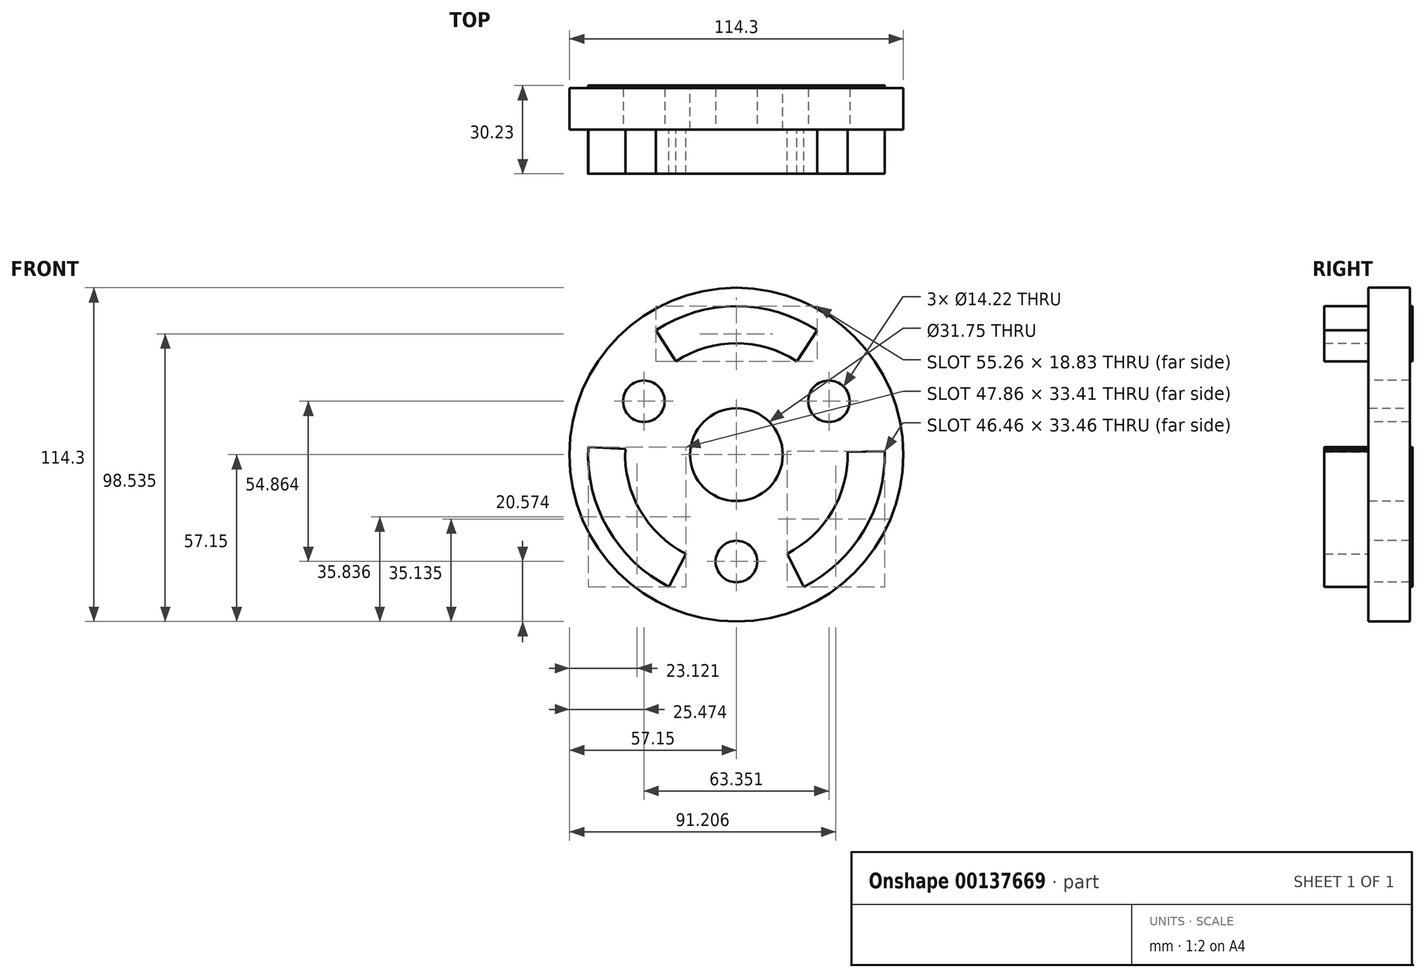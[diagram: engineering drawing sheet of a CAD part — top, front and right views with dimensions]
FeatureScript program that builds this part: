
annotation { "Feature Type Name" : "Feature", "Feature Type Description" : "" }
export const myFeature = defineFeature(function(context is Context, id is Id, definition is map)
    precondition{}
    {
        {
            var Q0;
            Q0=qCreatedBy(makeId("Front.planeOp"),FACE);
            var sketch = newSketch(context, id + "F0", { "sketchPlane" : qUnion([Q0])});
            skCircle(sketch, "E0", {"center": v(0, 0) * mm, "radius": 57.15 * mm});
            skCircle(sketch, "E1", {"center": v(0, 0) * mm, "radius": 15.88 * mm});
            skSolve(sketch);
        }
        {
            var Q0;
            Q0=makeQuery(id+"F0.imprint","IMPRINT",FACE,{"disambiguationData":[TD([[makeQuery(id+"F0.imprint","IMPRINT",EDGE,{"derivedFrom":sQuery(id+"F0.wireOp",EDGE,"E0")}),1.0]])]});
            extrude(context, id + "F1", {"entities" : qUnion([Q0]), "endBound" : BoundingType.SYMMETRIC, "depth" : 14.22 * mm});
        }
        {
            var Q0;
            Q0=makeQuery(id+"F1.opExtrude","CAP_FACE",FACE,{"disambiguationData":[OSD([sQuery(id+"F0.wireOp",EDGE,"E0"),sQuery(id+"F0.wireOp",EDGE,"E1")])],"isStart":false});
            var sketch = newSketch(context, id + "F2", { "sketchPlane" : qUnion([Q0])});
            skArc(sketch, "E2", {"start": v(-38.05, 1.96) * mm, "mid": v(-33, -19.05) * mm, "end": v(-17.33, -33.93) * mm});
            skCircle(sketch, "E3", {"center": v(0, -36.58) * mm, "radius": 7.11 * mm});
            skCircle(sketch, "E4.0", {"center": v(0, 0) * mm, "radius": 50.8 * mm});
            skCircle(sketch, "E5.1.1", {"center": v(31.68, 18.29) * mm, "radius": 7.11 * mm});
            skCircle(sketch, "E5.2.1", {"center": v(-31.68, 18.29) * mm, "radius": 7.11 * mm});
            skLineSegment(sketch, "E6", {"start": v(20.72, 31.97) * mm, "end": v(27.63, 42.63) * mm});
            skLineSegment(sketch, "E7", {"start": v(38.09, 0.91) * mm, "end": v(50.79, 1.21) * mm});
            skLineSegment(sketch, "E8", {"start": v(17.33, -33.93) * mm, "end": v(23.1, -45.24) * mm});
            skLineSegment(sketch, "E9", {"start": v(-17.33, -33.93) * mm, "end": v(-23.1, -45.24) * mm});
            skLineSegment(sketch, "E10", {"start": v(-38.05, 1.96) * mm, "end": v(-50.73, 2.62) * mm});
            skLineSegment(sketch, "E11", {"start": v(-20.72, 31.97) * mm, "end": v(-27.63, 42.63) * mm});
            skArc(sketch, "E12.trimOffspring", {"start": v(20.72, 31.97) * mm, "mid": v(0, 38.1) * mm, "end": v(-20.72, 31.97) * mm});
            skArc(sketch, "E13.trimOffspring", {"start": v(17.33, -33.93) * mm, "mid": v(32.73, -19.5) * mm, "end": v(38.09, 0.91) * mm});
            skSolve(sketch);
        }
        {
            var Q0;
            Q0=makeQuery(id+"F2.imprint","IMPRINT",FACE,{"disambiguationData":[TD([[makeQuery(id+"F2.imprint","IMPRINT",EDGE,{"derivedFrom":sQuery(id+"F2.wireOp",EDGE,"E2")}),-1.0]])]});
            var Q1;
            {var subQ0=sQuery(id+"F2.wireOp",EDGE,"E6");Q1=makeQuery(id+"F2.imprint","IMPRINT",FACE,{"disambiguationData":[TD([[makeQuery(id+"F2.imprint","IMPRINT",EDGE,{"derivedFrom":subQ0}),1.0]])]});}
            var Q2;
            {var subQ0=sQuery(id+"F2.wireOp",EDGE,"E7");Q2=makeQuery(id+"F2.imprint","IMPRINT",FACE,{"disambiguationData":[TD([[makeQuery(id+"F2.imprint","IMPRINT",EDGE,{"derivedFrom":subQ0}),-1.0]])]});}
            extrude(context, id + "F3", {"entities" : qUnion([Q0, Q1, Q2]), "operationType" : NewBodyOperationType.ADD, "endBound" : BoundingType.SYMMETRIC, "depth" : 30.23 * mm});
        }
        {
            var Q0;
            Q0=makeQuery(id+"F2.imprint","IMPRINT",FACE,{"disambiguationData":[TD([[makeQuery(id+"F2.imprint","IMPRINT",EDGE,{"derivedFrom":sQuery(id+"F2.wireOp",EDGE,"E5.2.1")}),1.0]])]});
            var Q1;
            Q1=makeQuery(id+"F2.imprint","IMPRINT",FACE,{"disambiguationData":[TD([[makeQuery(id+"F2.imprint","IMPRINT",EDGE,{"derivedFrom":sQuery(id+"F2.wireOp",EDGE,"E5.1.1")}),1.0]])]});
            var Q2;
            Q2=makeQuery(id+"F2.imprint","IMPRINT",FACE,{"disambiguationData":[TD([[makeQuery(id+"F2.imprint","IMPRINT",EDGE,{"derivedFrom":sQuery(id+"F2.wireOp",EDGE,"E3")}),1.0]])]});
            extrude(context, id + "F4", {"entities" : qUnion([Q0, Q1, Q2]), "operationType" : NewBodyOperationType.REMOVE, "endBound" : BoundingType.THROUGH_ALL, "oppositeDirection" : true, "depth" : 25.4 * mm});
        }
    });
